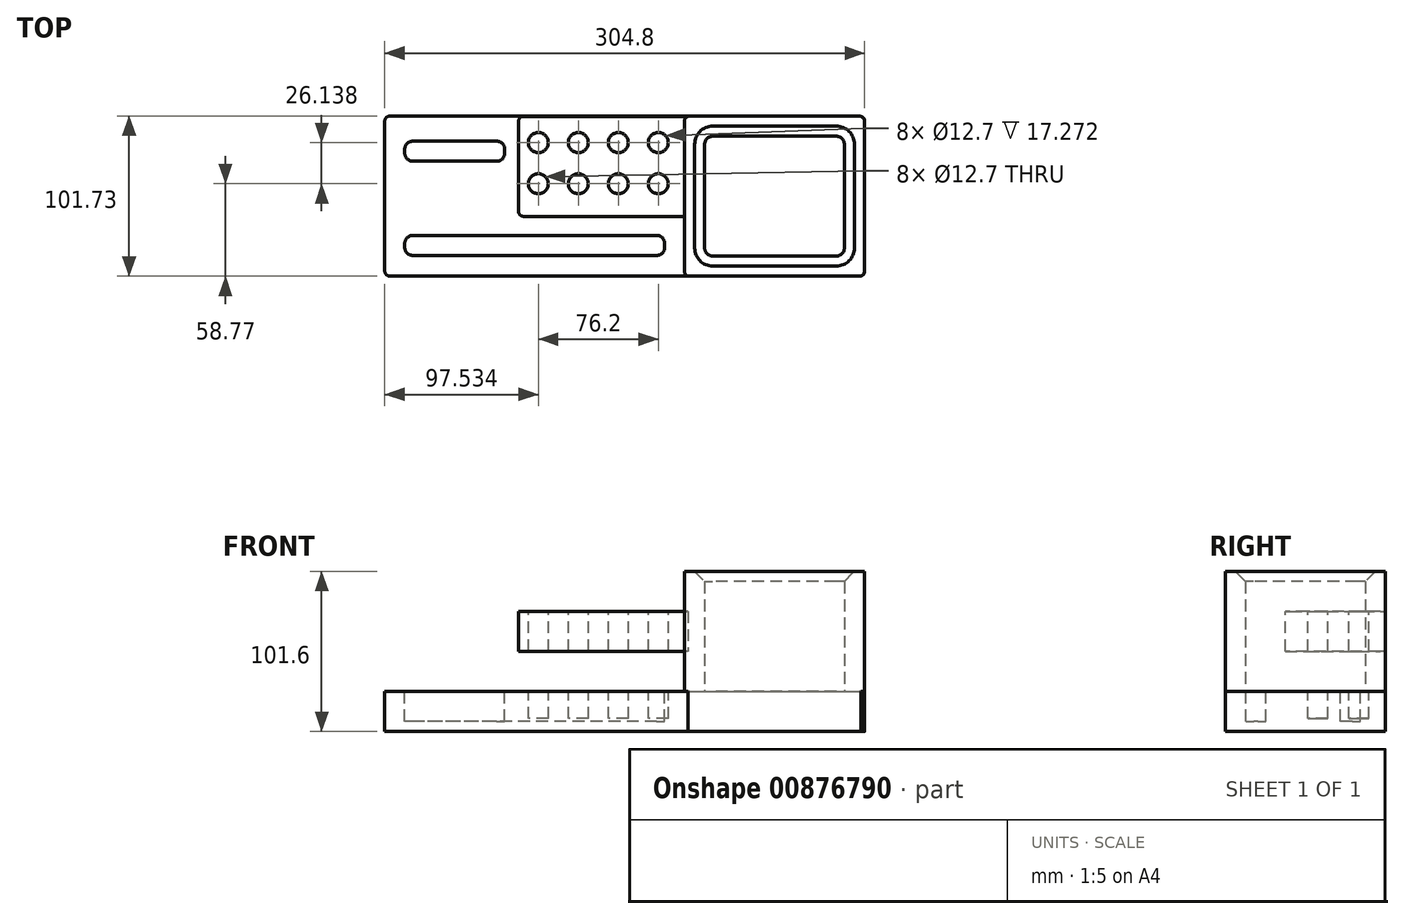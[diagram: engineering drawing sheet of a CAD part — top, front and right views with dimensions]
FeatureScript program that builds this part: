
annotation { "Feature Type Name" : "Feature", "Feature Type Description" : "" }
export const myFeature = defineFeature(function(context is Context, id is Id, definition is map)
    precondition{}
    {
        {
            var Q0;
            Q0=qCreatedBy(makeId("Top.planeOp"),FACE);
            var sketch = newSketch(context, id + "F0", { "sketchPlane" : qUnion([Q0])});
            skLineSegment(sketch, "E0", {"start": v(-63.83, 42.96) * mm, "end": v(240.97, 42.96) * mm});
            skLineSegment(sketch, "E1", {"start": v(240.97, 42.96) * mm, "end": v(240.97, -58.64) * mm});
            skLineSegment(sketch, "E2", {"start": v(240.97, -58.64) * mm, "end": v(-63.83, -58.64) * mm});
            skLineSegment(sketch, "E3", {"start": v(-63.83, -58.64) * mm, "end": v(-63.83, 42.96) * mm});
            skLineSegment(sketch, "E4", {"start": v(126.67, 42.96) * mm, "end": v(126.67, -58.64) * mm});
            skLineSegment(sketch, "E5", {"start": v(139.37, 30.25) * mm, "end": v(139.37, -45.94) * mm});
            skLineSegment(sketch, "E6", {"start": v(139.37, -45.94) * mm, "end": v(228.27, -45.94) * mm});
            skLineSegment(sketch, "E7", {"start": v(139.37, 30.25) * mm, "end": v(228.27, 30.25) * mm});
            skLineSegment(sketch, "E8", {"start": v(228.27, 30.25) * mm, "end": v(228.27, -45.94) * mm});
            skSolve(sketch);
        }
        {
            var Q0;
            Q0 = qSketchRegion(id + "F0", true);
            var Q1;
            Q1=makeQuery(id+"F0.imprint","IMPRINT",FACE,{"disambiguationData":[TD([[makeQuery(id+"F0.imprint","IMPRINT",EDGE,{"derivedFrom":sQuery(id+"F0.wireOp",EDGE,"E5")}),1.0]])]});
            extrude(context, id + "F1", {"entities" : qUnion([Q0, Q1]), "depth" : 25.4 * mm, "offsetDistance" : 25.4 * mm});
        }
        {
            var Q0;
            Q0=qCreatedBy(makeId("Top.planeOp"),FACE);
            var sketch = newSketch(context, id + "F2", { "sketchPlane" : qUnion([Q0])});
            skLineSegment(sketch, "E9", {"start": v(126.49, 42.88) * mm, "end": v(126.49, -58.77) * mm});
            skLineSegment(sketch, "E10", {"start": v(126.49, -58.77) * mm, "end": v(240.79, -58.77) * mm});
            skLineSegment(sketch, "E11", {"start": v(240.79, -58.77) * mm, "end": v(240.79, 42.88) * mm});
            skLineSegment(sketch, "E12", {"start": v(240.79, 42.88) * mm, "end": v(126.49, 42.88) * mm});
            skLineSegment(sketch, "E13", {"start": v(139.37, 30.18) * mm, "end": v(139.37, -45.94) * mm});
            skLineSegment(sketch, "E14", {"start": v(139.37, -45.94) * mm, "end": v(228.09, -45.94) * mm});
            skLineSegment(sketch, "E15", {"start": v(228.09, -45.94) * mm, "end": v(228.09, 30.18) * mm});
            skLineSegment(sketch, "E16", {"start": v(228.09, 30.18) * mm, "end": v(139.37, 30.18) * mm});
            skSolve(sketch);
        }
        {
            var Q0;
            Q0 = qSketchRegion(id + "F2", true);
            extrude(context, id + "F3", {"entities" : qUnion([Q0]), "operationType" : NewBodyOperationType.ADD, "depth" : 101.6 * mm, "offsetDistance" : 25.4 * mm});
        }
        {
            var Q0;
            Q0=qCreatedBy(makeId("Right.planeOp"),FACE);
            var sketch = newSketch(context, id + "F4", { "sketchPlane" : qUnion([Q0])});
            skLineSegment(sketch, "E17", {"start": v(42.79, 76.36) * mm, "end": v(-20.71, 76.36) * mm});
            skLineSegment(sketch, "E18", {"start": v(-20.71, 76.36) * mm, "end": v(-20.71, 50.96) * mm});
            skLineSegment(sketch, "E19", {"start": v(-20.71, 50.96) * mm, "end": v(42.79, 50.96) * mm});
            skLineSegment(sketch, "E20", {"start": v(42.79, 50.96) * mm, "end": v(42.79, 76.36) * mm});
            skSolve(sketch);
        }
        {
            var Q0;
            Q0 = qSketchRegion(id + "F4", true);
            var Q1;
            Q1=makeQuery(id+"F3.opExtrude","SWEPT_FACE",FACE,{"disambiguationData":[OSD([sQuery(id+"F2.wireOp",EDGE,"E9")])]});
            extrude(context, id + "F5", {"entities" : qUnion([Q0]), "operationType" : NewBodyOperationType.ADD, "endBound" : BoundingType.UP_TO_SURFACE, "depth" : 25.4 * mm, "endBoundEntityFace" : qUnion([Q1]), "offsetDistance" : 25.4 * mm});
        }
        {
            var Q0;
            Q0=qCreatedBy(makeId("Front.planeOp"),FACE);
            var sketch = newSketch(context, id + "F6", { "sketchPlane" : qUnion([Q0])});
            skLineSegment(sketch, "E21", {"start": v(21.14, 78.33) * mm, "end": v(21.14, 48.28) * mm});
            skLineSegment(sketch, "E22", {"start": v(21.14, 48.28) * mm, "end": v(0, 48.28) * mm});
            skLineSegment(sketch, "E23", {"start": v(0, 48.28) * mm, "end": v(0, 78.33) * mm});
            skLineSegment(sketch, "E24", {"start": v(0, 78.33) * mm, "end": v(21.14, 78.33) * mm});
            skSolve(sketch);
        }
        {
            var Q0;
            Q0 = qSketchRegion(id + "F6", true);
            extrude(context, id + "F7", {"entities" : qUnion([Q0]), "operationType" : NewBodyOperationType.REMOVE, "endBound" : BoundingType.SYMMETRIC, "oppositeDirection" : true, "depth" : 217.42 * mm, "offsetDistance" : 25.4 * mm});
        }
        {
            var Q0;
            {var subQ0=sQuery(id+"F0.wireOp",EDGE,"E3");Q0=makeQuery(id+"F0.imprint","IMPRINT",FACE,{"disambiguationData":[TD([[makeQuery(id+"F0.imprint","IMPRINT",EDGE,{"derivedFrom":subQ0}),-1.0]])]});}
            cPlane(context, id + "F8", {"entities" : qUnion([Q0]), "cplaneType" : CPlaneType.OFFSET, "offset" : 25.4 * mm, "width" : 152.4 * mm, "height" : 152.4 * mm});
        }
        {
            var Q0;
            Q0=qCreatedBy(id+"F8.planeOp",FACE);
            var sketch = newSketch(context, id + "F9", { "sketchPlane" : qUnion([Q0])});
            skLineSegment(sketch, "E25", {"start": v(-51.13, 27.02) * mm, "end": v(-51.13, 14.32) * mm});
            skLineSegment(sketch, "E26", {"start": v(-51.13, 14.32) * mm, "end": v(12.38, 14.32) * mm});
            skLineSegment(sketch, "E27", {"start": v(12.38, 14.32) * mm, "end": v(12.38, 27.02) * mm});
            skLineSegment(sketch, "E28", {"start": v(12.38, 27.02) * mm, "end": v(-51.13, 27.02) * mm});
            skLineSegment(sketch, "E29", {"start": v(-51.13, -32.84) * mm, "end": v(-51.13, -45.54) * mm});
            skLineSegment(sketch, "E30", {"start": v(-51.13, -45.54) * mm, "end": v(113.97, -45.54) * mm});
            skLineSegment(sketch, "E31", {"start": v(113.97, -45.54) * mm, "end": v(113.97, -32.84) * mm});
            skLineSegment(sketch, "E32", {"start": v(113.97, -32.84) * mm, "end": v(-51.13, -32.84) * mm});
            skSolve(sketch);
        }
        {
            var Q0;
            Q0 = qSketchRegion(id + "F9", true);
            extrude(context, id + "F10", {"entities" : qUnion([Q0]), "operationType" : NewBodyOperationType.REMOVE, "oppositeDirection" : true, "depth" : 19.05 * mm, "offsetDistance" : 25.4 * mm});
        }
        {
            var Q0;
            {var subQ0=sQuery(id+"F0.wireOp",EDGE,"E3");Q0=makeQuery(id+"F0.imprint","IMPRINT",FACE,{"disambiguationData":[TD([[makeQuery(id+"F0.imprint","IMPRINT",EDGE,{"derivedFrom":subQ0}),-1.0]])]});}
            cPlane(context, id + "F11", {"entities" : qUnion([Q0]), "cplaneType" : CPlaneType.OFFSET, "offset" : 78.74 * mm, "width" : 152.4 * mm, "height" : 152.4 * mm});
        }
        {
            var Q0;
            Q0=qCreatedBy(id+"F11.planeOp",FACE);
            var sketch = newSketch(context, id + "F12", { "sketchPlane" : qUnion([Q0])});
            skCircle(sketch, "E33", {"center": v(33.7, 26.14) * mm, "radius": 6.35 * mm});
            skCircle(sketch, "E34", {"center": v(59.1, 26.14) * mm, "radius": 6.35 * mm});
            skCircle(sketch, "E35", {"center": v(84.5, 26.14) * mm, "radius": 6.35 * mm});
            skCircle(sketch, "E36", {"center": v(109.9, 26.14) * mm, "radius": 6.35 * mm});
            skCircle(sketch, "E37", {"center": v(109.9, 0) * mm, "radius": 6.35 * mm});
            skCircle(sketch, "E38", {"center": v(84.5, 0) * mm, "radius": 6.35 * mm});
            skCircle(sketch, "E39", {"center": v(59.1, 0) * mm, "radius": 6.35 * mm});
            skCircle(sketch, "E40", {"center": v(33.7, 0) * mm, "radius": 6.35 * mm});
            skSolve(sketch);
        }
        {
            var Q0;
            Q0 = qSketchRegion(id + "F12", true);
            extrude(context, id + "F13", {"entities" : qUnion([Q0]), "operationType" : NewBodyOperationType.REMOVE, "oppositeDirection" : true, "depth" : 70.61 * mm, "offsetDistance" : 25.4 * mm});
        }
        {
            var Q0;
            Q0=makeQuery(id+"F7.boolean.opBoolean","INTERSECT",EDGE,{"derivedFrom":[makeQuery(id+"F5.opExtrude","SWEPT_FACE",FACE,{"disambiguationData":[OSD([sQuery(id+"F4.wireOp",EDGE,"E18")])]}),makeQuery(id+"F7.opExtrude","SWEPT_FACE",FACE,{"disambiguationData":[OSD([sQuery(id+"F6.wireOp",EDGE,"E21")])]})]});
            var Q1;
            Q1=makeQuery(id+"F7.boolean.opBoolean","INTERSECT",EDGE,{"derivedFrom":[makeQuery(id+"F5.opExtrude","SWEPT_FACE",FACE,{"disambiguationData":[OSD([sQuery(id+"F4.wireOp",EDGE,"E20")])]}),makeQuery(id+"F7.opExtrude","SWEPT_FACE",FACE,{"disambiguationData":[OSD([sQuery(id+"F6.wireOp",EDGE,"E21")])]})]});
            var Q2;
            Q2=makeQuery(id+"F3.opExtrude","SWEPT_EDGE",EDGE,{"disambiguationData":[OSD([sQuery(id+"F2.wireOp",EDGE,"E9"),sQuery(id+"F2.wireOp",EDGE,"E10")])]});
            var Q3;
            Q3=makeQuery(id+"F1.opExtrude","SWEPT_EDGE",EDGE,{"disambiguationData":[OSD([sQuery(id+"F0.wireOp",EDGE,"E0"),sQuery(id+"F0.wireOp",EDGE,"E1")])]});
            var Q4;
            Q4=makeQuery(id+"F3.opExtrude","SWEPT_EDGE",EDGE,{"disambiguationData":[OSD([sQuery(id+"F2.wireOp",EDGE,"E11"),sQuery(id+"F2.wireOp",EDGE,"E12")])]});
            var Q5;
            Q5=makeQuery(id+"F3.opExtrude","SWEPT_EDGE",EDGE,{"disambiguationData":[OSD([sQuery(id+"F2.wireOp",EDGE,"E9"),sQuery(id+"F2.wireOp",EDGE,"E12")])]});
            var Q6;
            Q6=makeQuery(id+"F3.opExtrude","SWEPT_EDGE",EDGE,{"disambiguationData":[OSD([sQuery(id+"F2.wireOp",EDGE,"E10"),sQuery(id+"F2.wireOp",EDGE,"E11")])]});
            fillet(context, id + "F14", {"entities" : qUnion([Q0, Q1, Q2, Q3, Q4, Q5, Q6]), "radius" : 3.17 * mm, "tangentPropagation" : true, "allowEdgeOverflow" : false});
        }
        {
            var Q0;
            Q0=makeQuery(id+"F1.opExtrude","SWEPT_EDGE",EDGE,{"disambiguationData":[OSD([sQuery(id+"F0.wireOp",EDGE,"E1"),sQuery(id+"F0.wireOp",EDGE,"E2")])]});
            var Q1;
            Q1=makeQuery(id+"F1.opExtrude","SWEPT_EDGE",EDGE,{"disambiguationData":[OSD([sQuery(id+"F0.wireOp",EDGE,"E2"),sQuery(id+"F0.wireOp",EDGE,"E3")])]});
            var Q2;
            Q2=makeQuery(id+"F1.opExtrude","SWEPT_EDGE",EDGE,{"disambiguationData":[OSD([sQuery(id+"F0.wireOp",EDGE,"E0"),sQuery(id+"F0.wireOp",EDGE,"E3")])]});
            fillet(context, id + "F15", {"entities" : qUnion([Q0, Q1, Q2]), "radius" : 3.17 * mm, "tangentPropagation" : true, "allowEdgeOverflow" : false});
        }
        {
            var Q0;
            Q0=makeQuery(id+"F10.boolean.opBoolean","COPY",EDGE,{"derivedFrom":makeQuery(id+"F10.opExtrude","SWEPT_EDGE",EDGE,{"disambiguationData":[OSD([sQuery(id+"F9.wireOp",EDGE,"E27"),sQuery(id+"F9.wireOp",EDGE,"E28")])]})});
            var Q1;
            Q1=makeQuery(id+"F10.boolean.opBoolean","COPY",EDGE,{"derivedFrom":makeQuery(id+"F10.opExtrude","SWEPT_EDGE",EDGE,{"disambiguationData":[OSD([sQuery(id+"F9.wireOp",EDGE,"E26"),sQuery(id+"F9.wireOp",EDGE,"E27")])]})});
            var Q2;
            Q2=makeQuery(id+"F10.boolean.opBoolean","COPY",EDGE,{"derivedFrom":makeQuery(id+"F10.opExtrude","SWEPT_EDGE",EDGE,{"disambiguationData":[OSD([sQuery(id+"F9.wireOp",EDGE,"E25"),sQuery(id+"F9.wireOp",EDGE,"E28")])]})});
            var Q3;
            Q3=makeQuery(id+"F10.boolean.opBoolean","COPY",EDGE,{"derivedFrom":makeQuery(id+"F10.opExtrude","SWEPT_EDGE",EDGE,{"disambiguationData":[OSD([sQuery(id+"F9.wireOp",EDGE,"E25"),sQuery(id+"F9.wireOp",EDGE,"E26")])]})});
            var Q4;
            Q4=makeQuery(id+"F10.boolean.opBoolean","COPY",EDGE,{"derivedFrom":makeQuery(id+"F10.opExtrude","SWEPT_EDGE",EDGE,{"disambiguationData":[OSD([sQuery(id+"F9.wireOp",EDGE,"E29"),sQuery(id+"F9.wireOp",EDGE,"E32")])]})});
            var Q5;
            Q5=makeQuery(id+"F10.boolean.opBoolean","COPY",EDGE,{"derivedFrom":makeQuery(id+"F10.opExtrude","SWEPT_EDGE",EDGE,{"disambiguationData":[OSD([sQuery(id+"F9.wireOp",EDGE,"E29"),sQuery(id+"F9.wireOp",EDGE,"E30")])]})});
            var Q6;
            Q6=makeQuery(id+"F10.boolean.opBoolean","COPY",EDGE,{"derivedFrom":makeQuery(id+"F10.opExtrude","SWEPT_EDGE",EDGE,{"disambiguationData":[OSD([sQuery(id+"F9.wireOp",EDGE,"E31"),sQuery(id+"F9.wireOp",EDGE,"E32")])]})});
            var Q7;
            Q7=makeQuery(id+"F10.boolean.opBoolean","COPY",EDGE,{"derivedFrom":makeQuery(id+"F10.opExtrude","SWEPT_EDGE",EDGE,{"disambiguationData":[OSD([sQuery(id+"F9.wireOp",EDGE,"E30"),sQuery(id+"F9.wireOp",EDGE,"E31")])]})});
            var Q8;
            Q8=makeQuery(id+"F5.opExtrude","CAP_EDGE",EDGE,{"disambiguationData":[OSD([sQuery(id+"F4.wireOp",EDGE,"E18")])],"isStart":false});
            var Q9;
            Q9=makeQuery(id+"F3.opExtrude","SWEPT_EDGE",EDGE,{"disambiguationData":[OSD([sQuery(id+"F2.wireOp",EDGE,"E13"),sQuery(id+"F2.wireOp",EDGE,"E16")])]});
            var Q10;
            Q10=makeQuery(id+"F3.opExtrude","SWEPT_EDGE",EDGE,{"disambiguationData":[OSD([sQuery(id+"F2.wireOp",EDGE,"E13"),sQuery(id+"F2.wireOp",EDGE,"E14")])]});
            var Q11;
            Q11=makeQuery(id+"F3.opExtrude","SWEPT_EDGE",EDGE,{"disambiguationData":[OSD([sQuery(id+"F2.wireOp",EDGE,"E15"),sQuery(id+"F2.wireOp",EDGE,"E16")])]});
            var Q12;
            Q12=makeQuery(id+"F3.opExtrude","SWEPT_EDGE",EDGE,{"disambiguationData":[OSD([sQuery(id+"F2.wireOp",EDGE,"E14"),sQuery(id+"F2.wireOp",EDGE,"E15")])]});
            fillet(context, id + "F16", {"entities" : qUnion([Q0, Q1, Q2, Q3, Q4, Q5, Q6, Q7, Q8, Q9, Q10, Q11, Q12]), "radius" : 5.08 * mm, "tangentPropagation" : true, "allowEdgeOverflow" : false});
        }
        {
            var Q0;
            Q0=makeQuery(id+"F3.opExtrude","CAP_EDGE",EDGE,{"disambiguationData":[OSD([sQuery(id+"F2.wireOp",EDGE,"E13")])],"isStart":false});
            chamfer(context, id + "F17", {"entities" : qUnion([Q0]), "width" : 6.35 * mm, "tangentPropagation" : true});
        }
    });
